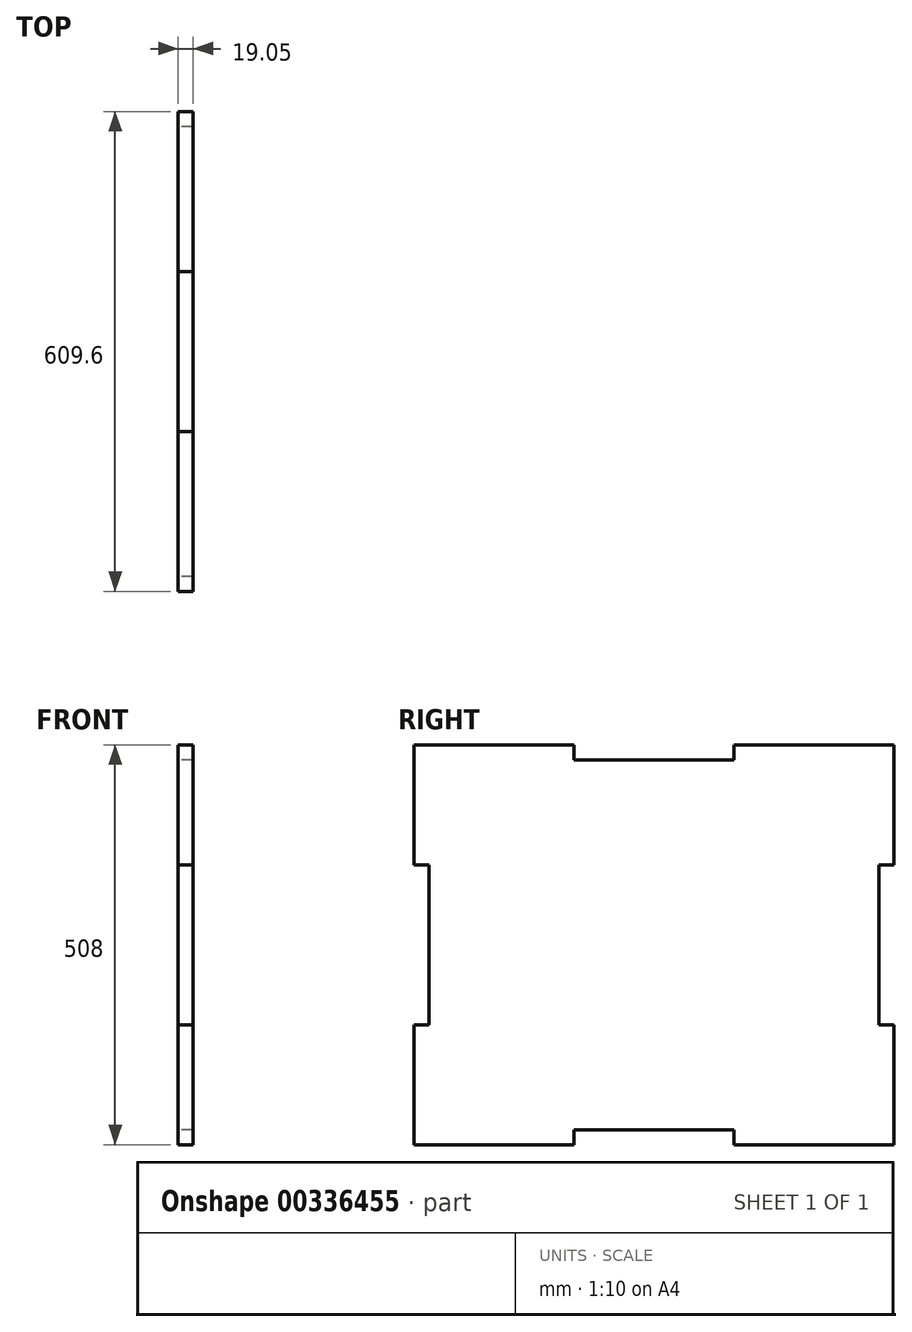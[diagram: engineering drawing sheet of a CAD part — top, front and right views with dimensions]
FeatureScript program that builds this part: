
annotation { "Feature Type Name" : "Feature", "Feature Type Description" : "" }
export const myFeature = defineFeature(function(context is Context, id is Id, definition is map)
    precondition{}
    {
        {
            var Q0;
            Q0=qCreatedBy(makeId("Right.planeOp"),FACE);
            var sketch = newSketch(context, id + "F0", { "sketchPlane" : qUnion([Q0])});
            skLineSegment(sketch, "E0.bottom", {"start": v(-428.85, 282.98) * mm, "end": v(180.75, 282.98) * mm});
            skLineSegment(sketch, "E0.top", {"start": v(-428.85, -225.02) * mm, "end": v(180.75, -225.02) * mm});
            skLineSegment(sketch, "E0.left", {"start": v(-428.85, 282.98) * mm, "end": v(-428.85, -225.02) * mm});
            skLineSegment(sketch, "E0.right", {"start": v(180.75, 282.98) * mm, "end": v(180.75, -225.02) * mm});
            skLineSegment(sketch, "E1.bottom", {"start": v(-22.45, 263.93) * mm, "end": v(-225.65, 263.93) * mm});
            skLineSegment(sketch, "E1.top", {"start": v(-22.45, 282.98) * mm, "end": v(-225.65, 282.98) * mm});
            skLineSegment(sketch, "E1.left", {"start": v(-22.45, 263.93) * mm, "end": v(-22.45, 282.98) * mm});
            skLineSegment(sketch, "E1.right", {"start": v(-225.65, 263.93) * mm, "end": v(-225.65, 282.98) * mm});
            skPoint(sketch, "E1.middle", {"position": v(-124.05, 273.46) * mm});
            skLineSegment(sketch, "E2.bottom", {"start": v(-22.45, -225.02) * mm, "end": v(-225.65, -225.02) * mm});
            skLineSegment(sketch, "E2.top", {"start": v(-22.45, -205.97) * mm, "end": v(-225.65, -205.97) * mm});
            skLineSegment(sketch, "E2.left", {"start": v(-22.45, -225.02) * mm, "end": v(-22.45, -205.97) * mm});
            skLineSegment(sketch, "E2.right", {"start": v(-225.65, -225.02) * mm, "end": v(-225.65, -205.97) * mm});
            skPoint(sketch, "E2.middle", {"position": v(-124.05, -215.5) * mm});
            skLineSegment(sketch, "E3.bottom", {"start": v(-409.8, -72.62) * mm, "end": v(-428.85, -72.62) * mm});
            skLineSegment(sketch, "E3.top", {"start": v(-409.8, 130.58) * mm, "end": v(-428.85, 130.58) * mm});
            skLineSegment(sketch, "E3.left", {"start": v(-409.8, -72.62) * mm, "end": v(-409.8, 130.58) * mm});
            skLineSegment(sketch, "E3.right", {"start": v(-428.85, -72.62) * mm, "end": v(-428.85, 130.58) * mm});
            skPoint(sketch, "E3.middle", {"position": v(-419.33, 28.98) * mm});
            skLineSegment(sketch, "E4.bottom", {"start": v(180.75, -72.62) * mm, "end": v(161.7, -72.62) * mm});
            skLineSegment(sketch, "E4.top", {"start": v(180.75, 130.58) * mm, "end": v(161.7, 130.58) * mm});
            skLineSegment(sketch, "E4.left", {"start": v(180.75, -72.62) * mm, "end": v(180.75, 130.58) * mm});
            skLineSegment(sketch, "E4.right", {"start": v(161.7, -72.62) * mm, "end": v(161.7, 130.58) * mm});
            skPoint(sketch, "E4.middle", {"position": v(171.22, 28.98) * mm});
            skSolve(sketch);
        }
        {
            var Q0;
            Q0=makeQuery(id+"F0.imprint","IMPRINT",FACE,{"disambiguationData":[TD([[makeQuery(id+"F0.imprint","IMPRINT",EDGE,{"derivedFrom":sQuery(id+"F0.wireOp",EDGE,"E0.top")}),1.0]])]});
            extrude(context, id + "F1", {"entities" : qUnion([Q0]), "depth" : 19.05 * mm});
        }
    });
